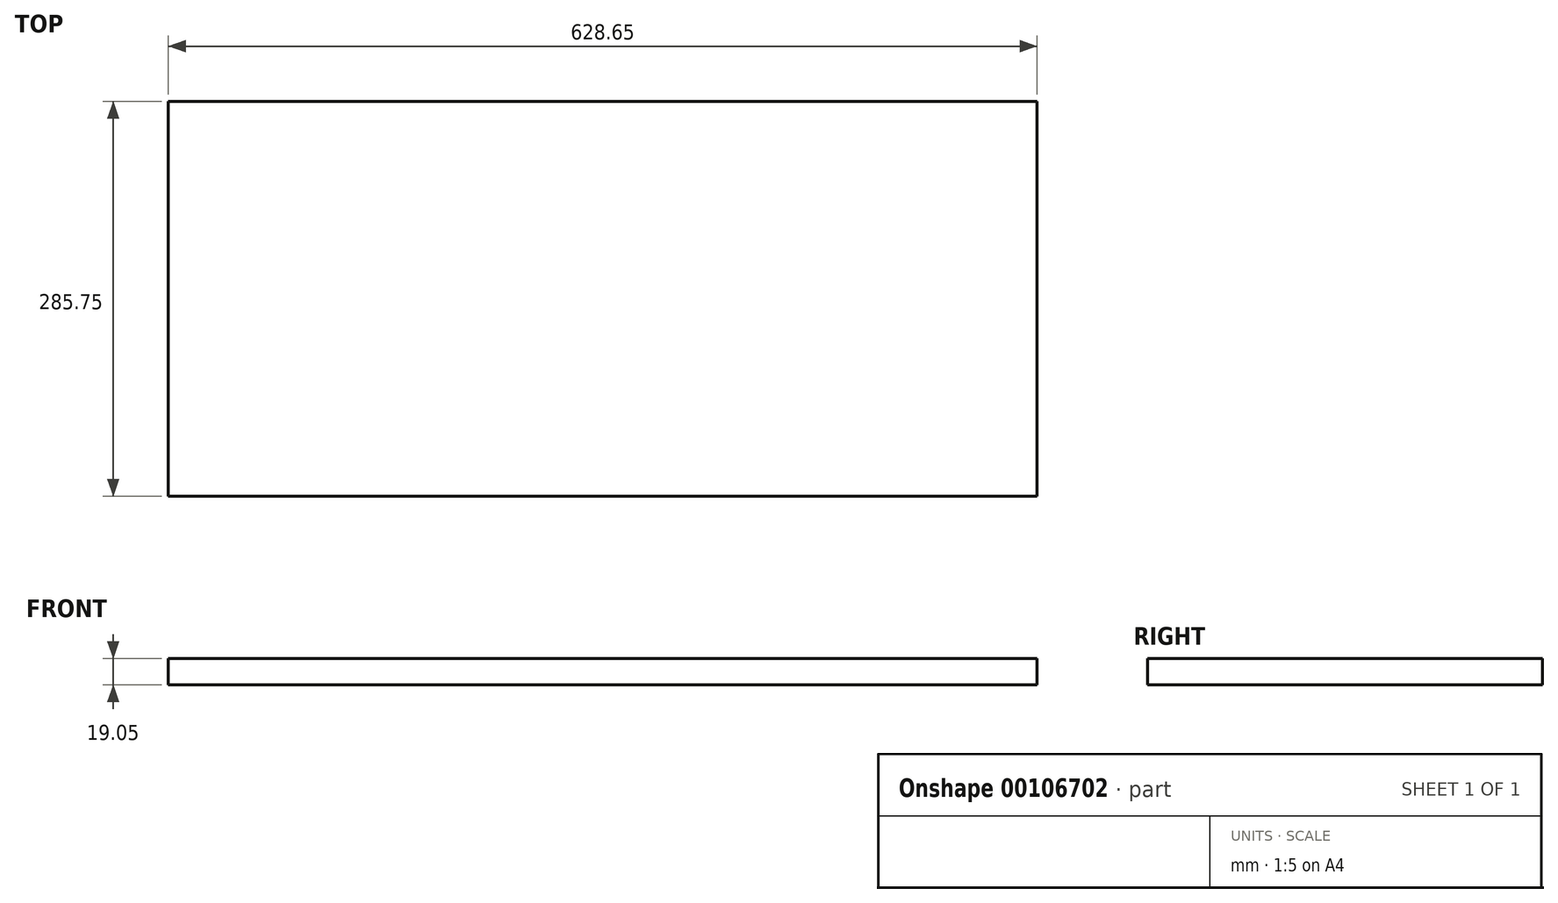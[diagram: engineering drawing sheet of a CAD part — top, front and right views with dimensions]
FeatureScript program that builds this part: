
annotation { "Feature Type Name" : "Feature", "Feature Type Description" : "" }
export const myFeature = defineFeature(function(context is Context, id is Id, definition is map)
    precondition{}
    {
        {
            var Q0;
            Q0=qCreatedBy(makeId("Top.planeOp"),FACE);
            var sketch = newSketch(context, id + "F0", { "sketchPlane" : qUnion([Q0])});
            skLineSegment(sketch, "E0.bottom", {"start": v(0, 0) * mm, "end": v(628.65, 0) * mm});
            skLineSegment(sketch, "E0.top", {"start": v(0, 285.75) * mm, "end": v(628.65, 285.75) * mm});
            skLineSegment(sketch, "E0.left", {"start": v(0, 0) * mm, "end": v(0, 285.75) * mm});
            skLineSegment(sketch, "E0.right", {"start": v(628.65, 0) * mm, "end": v(628.65, 285.75) * mm});
            skSolve(sketch);
        }
        {
            var Q0;
            Q0=makeQuery(id+"F0.imprint","IMPRINT",FACE,{"disambiguationData":[TD([[makeQuery(id+"F0.imprint","IMPRINT",EDGE,{"derivedFrom":sQuery(id+"F0.wireOp",EDGE,"E0.bottom")}),1.0]])]});
            extrude(context, id + "F1", {"entities" : qUnion([Q0]), "depth" : 19.05 * mm});
        }
    });
